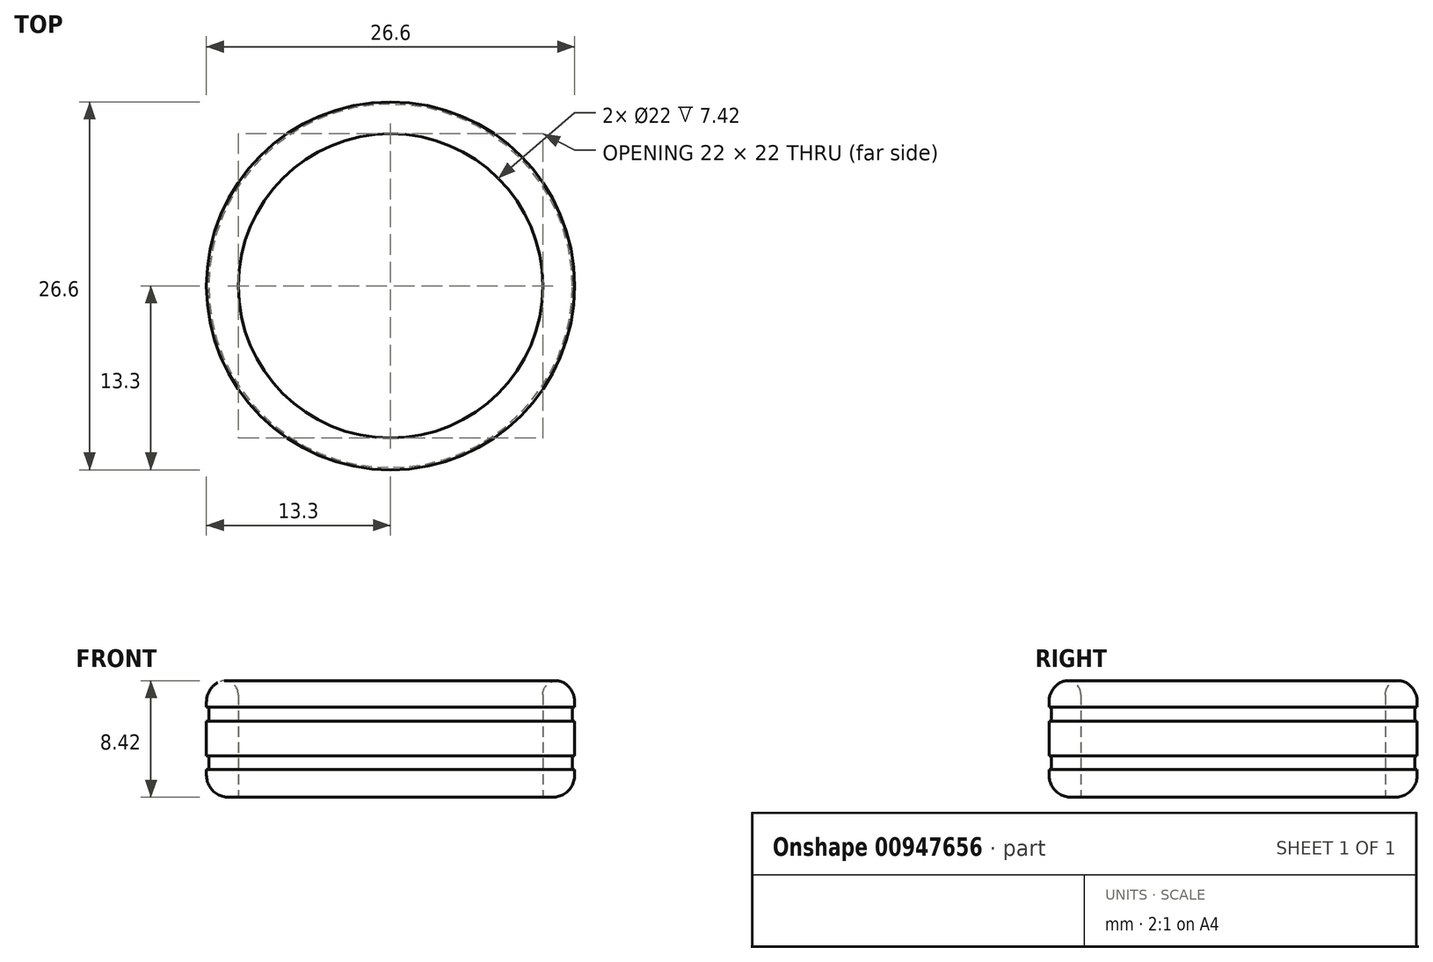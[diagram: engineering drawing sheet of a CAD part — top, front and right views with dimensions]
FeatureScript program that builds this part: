
annotation { "Feature Type Name" : "Feature", "Feature Type Description" : "" }
export const myFeature = defineFeature(function(context is Context, id is Id, definition is map)
    precondition{}
    {
        {
            var Q0;
            Q0=qCreatedBy(makeId("Top.planeOp"),FACE);
            var sketch = newSketch(context, id + "F0", { "sketchPlane" : qUnion([Q0])});
            skCircle(sketch, "E0", {"center": v(0, 0) * mm, "radius": 11 * mm});
            skCircle(sketch, "E1.0", {"center": v(0, 0) * mm, "radius": 13.3 * mm});
            skSolve(sketch);
        }
        {
            var Q0;
            Q0=makeQuery(id+"F0.imprint","IMPRINT",FACE,{"disambiguationData":[TD([[makeQuery(id+"F0.imprint","IMPRINT",EDGE,{"derivedFrom":sQuery(id+"F0.wireOp",EDGE,"E0")}),-1.0]])]});
            extrude(context, id + "F1", {"entities" : qUnion([Q0]), "depth" : 8.5 * mm, "offsetDistance" : 25 * mm});
        }
        {
            var Q0;
            Q0=makeQuery(id+"F1.opExtrude","CAP_EDGE",EDGE,{"disambiguationData":[OSD([sQuery(id+"F0.wireOp",EDGE,"E1.0")])],"isStart":false});
            var Q1;
            Q1=makeQuery(id+"F1.opExtrude","CAP_EDGE",EDGE,{"disambiguationData":[OSD([sQuery(id+"F0.wireOp",EDGE,"E1.0")])],"isStart":true});
            fillet(context, id + "F2", {"entities" : qUnion([Q0, Q1]), "radius" : 1.6 * mm, "tangentPropagation" : true, "allowEdgeOverflow" : false});
        }
        {
            var Q0;
            Q0=makeQuery(id+"F1.opExtrude","CAP_EDGE",EDGE,{"disambiguationData":[OSD([sQuery(id+"F0.wireOp",EDGE,"E0")])],"isStart":false});
            fillet(context, id + "F3", {"entities" : qUnion([Q0]), "radius" : 1 * mm, "tangentPropagation" : true, "allowEdgeOverflow" : false});
        }
        {
            var Q0;
            Q0=qCreatedBy(makeId("Front.planeOp"),FACE);
            var sketch = newSketch(context, id + "F4", { "sketchPlane" : qUnion([Q0])});
            skLineSegment(sketch, "E2.bottom", {"start": v(-13.94, 3) * mm, "end": v(-13.14, 3) * mm});
            skLineSegment(sketch, "E2.top", {"start": v(-13.94, 2) * mm, "end": v(-13.14, 2) * mm});
            skLineSegment(sketch, "E2.left", {"start": v(-13.94, 3) * mm, "end": v(-13.94, 2) * mm});
            skLineSegment(sketch, "E2.right", {"start": v(-13.14, 3) * mm, "end": v(-13.14, 2) * mm});
            skLineSegment(sketch, "E3.bottom", {"start": v(-13.94, 6.5) * mm, "end": v(-13.14, 6.5) * mm});
            skLineSegment(sketch, "E3.top", {"start": v(-13.94, 5.5) * mm, "end": v(-13.14, 5.5) * mm});
            skLineSegment(sketch, "E3.left", {"start": v(-13.94, 6.5) * mm, "end": v(-13.94, 5.5) * mm});
            skLineSegment(sketch, "E3.right", {"start": v(-13.14, 6.5) * mm, "end": v(-13.14, 5.5) * mm});
            skLineSegment(sketch, "E4", {"start": v(-13.94, 5.5) * mm, "end": v(-13.94, -3.61) * mm});
            skSolve(sketch);
        }
        {
            var Q0;
            Q0=makeQuery(id+"F4.imprint","IMPRINT",FACE,{"disambiguationData":[TD([[makeQuery(id+"F4.imprint","IMPRINT",EDGE,{"derivedFrom":sQuery(id+"F4.wireOp",EDGE,"E3.bottom")}),-1.0]])]});
            var Q1;
            {var subQ0=sQuery(id+"F4.wireOp",EDGE,"E2.bottom");Q1=makeQuery(id+"F4.imprint","IMPRINT",FACE,{"disambiguationData":[TD([[makeQuery(id+"F4.imprint","IMPRINT",EDGE,{"derivedFrom":subQ0}),-1.0]])]});}
            var Q2;
            {var subQ0=sQuery(id+"F0.wireOp",EDGE,"E1.0");Q2=makeQuery(id+"F2.opFillet","BLEND_EDGE",EDGE,{"blendedFrom":[makeQuery(id+"F1.opExtrude","CAP_EDGE",EDGE,{"disambiguationData":[OSD([subQ0])],"isStart":false}),makeQuery(id+"F1.opExtrude","SWEPT_FACE",FACE,{"disambiguationData":[OSD([subQ0])]})],"blendedInto":[makeQuery(id+"F1.opExtrude","SWEPT_FACE",FACE,{"disambiguationData":[OSD([subQ0])]})]});}
            sweep(context, id + "F5", {"operationType" : NewBodyOperationType.REMOVE, "profiles" : qUnion([Q0, Q1]), "path" : qUnion([Q2])});
        }
    });
